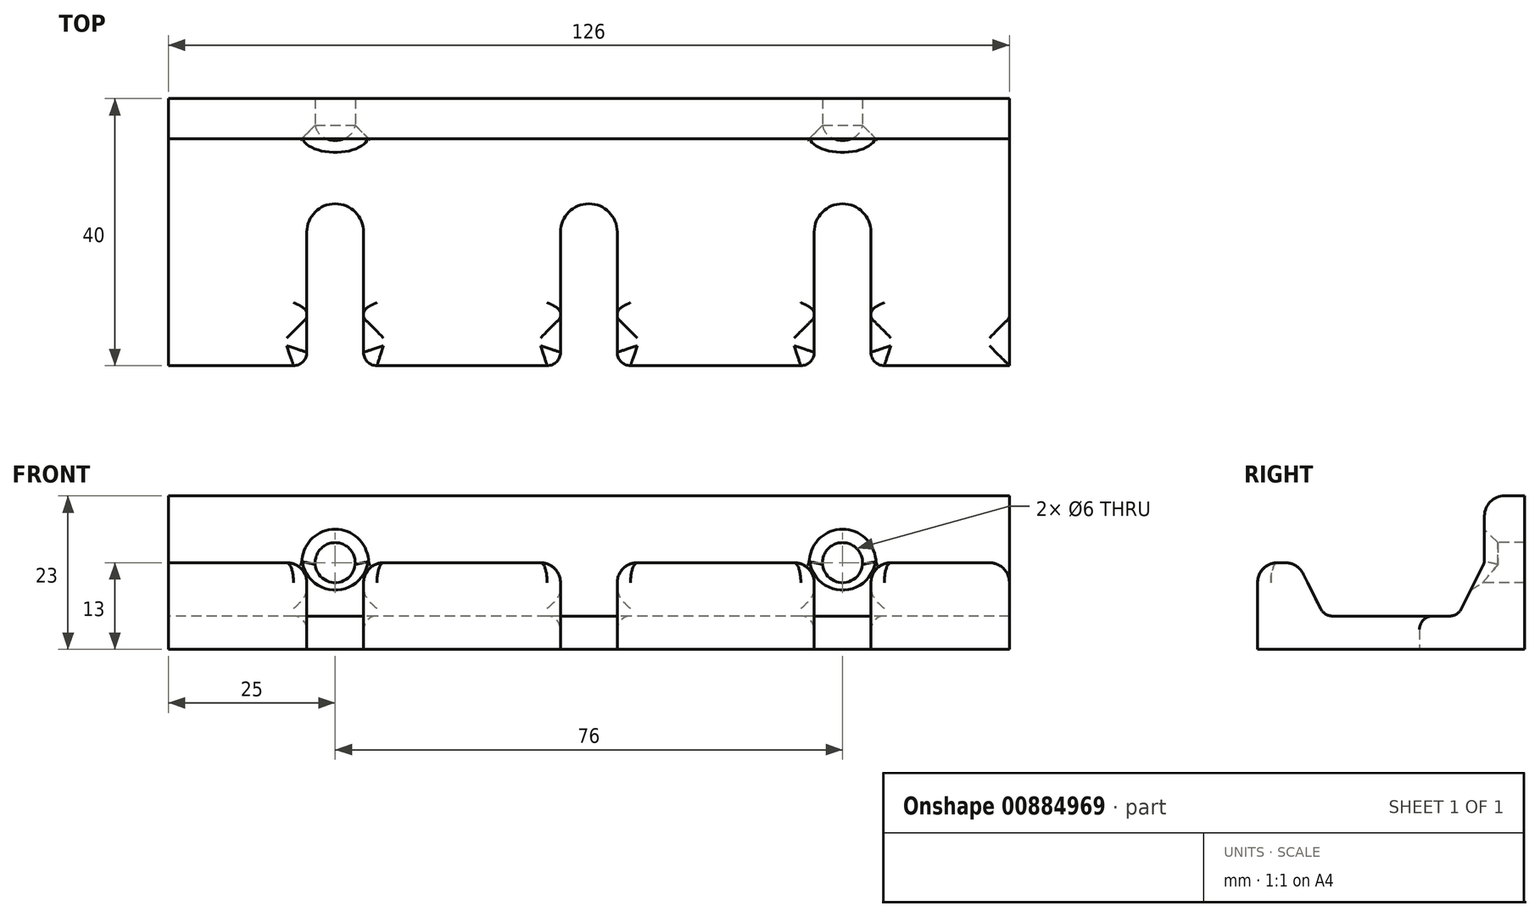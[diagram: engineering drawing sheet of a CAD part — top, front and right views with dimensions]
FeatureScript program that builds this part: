
annotation { "Feature Type Name" : "Feature", "Feature Type Description" : "" }
export const myFeature = defineFeature(function(context is Context, id is Id, definition is map)
    precondition{}
    {
        {
            var Q0;
            Q0=qCreatedBy(makeId("Top.planeOp"),FACE);
            var sketch = newSketch(context, id + "F0", { "sketchPlane" : qUnion([Q0])});
            skLineSegment(sketch, "E0.bottom", {"start": v(-63, 20) * mm, "end": v(63, 20) * mm});
            skLineSegment(sketch, "E0.top", {"start": v(-63, -20) * mm, "end": v(63, -20) * mm});
            skLineSegment(sketch, "E0.left", {"start": v(-63, 20) * mm, "end": v(-63, -20) * mm});
            skLineSegment(sketch, "E0.right", {"start": v(63, 20) * mm, "end": v(63, -20) * mm});
            skPoint(sketch, "E0.middle", {"position": v(0, 0) * mm});
            skSolve(sketch);
        }
        {
            var Q0;
            Q0=makeQuery(id+"F0.imprint","IMPRINT",FACE,{"disambiguationData":[TD([[makeQuery(id+"F0.imprint","IMPRINT",EDGE,{"derivedFrom":sQuery(id+"F0.wireOp",EDGE,"E0.bottom")}),-1.0]])]});
            extrude(context, id + "F1", {"entities" : qUnion([Q0]), "depth" : 5 * mm, "offsetDistance" : 25 * mm});
        }
        {
            var Q0;
            Q0=makeQuery(id+"F1.opExtrude","CAP_FACE",FACE,{"disambiguationData":[OSD([sQuery(id+"F0.wireOp",EDGE,"E0.bottom"),sQuery(id+"F0.wireOp",EDGE,"E0.top"),sQuery(id+"F0.wireOp",EDGE,"E0.left"),sQuery(id+"F0.wireOp",EDGE,"E0.right")])],"isStart":false});
            var sketch = newSketch(context, id + "F2", { "sketchPlane" : qUnion([Q0])});
            skLineSegment(sketch, "E1.bottom", {"start": v(-63, 10) * mm, "end": v(63, 10) * mm});
            skLineSegment(sketch, "E1.top", {"start": v(-63, -10) * mm, "end": v(63, -10) * mm});
            skLineSegment(sketch, "E1.left", {"start": v(-63, 10) * mm, "end": v(-63, -10) * mm});
            skLineSegment(sketch, "E1.right", {"start": v(63, 10) * mm, "end": v(63, -10) * mm});
            skPoint(sketch, "E1.middle", {"position": v(0, 0) * mm});
            skLineSegment(sketch, "E2.bottom", {"start": v(-63, 20) * mm, "end": v(63, 20) * mm});
            skLineSegment(sketch, "E2.top", {"start": v(-63, -20) * mm, "end": v(63, -20) * mm});
            skLineSegment(sketch, "E2.left", {"start": v(-63, 20) * mm, "end": v(-63, -20) * mm});
            skLineSegment(sketch, "E2.right", {"start": v(63, 20) * mm, "end": v(63, -20) * mm});
            skSolve(sketch);
        }
        {
            var Q0;
            {var subQ0=sQuery(id+"F2.wireOp",EDGE,"E1.bottom");Q0=makeQuery(id+"F2.imprint","IMPRINT",FACE,{"disambiguationData":[TD([[makeQuery(id+"F2.imprint","IMPRINT",EDGE,{"derivedFrom":subQ0}),1.0]])]});}
            var Q1;
            {var subQ0=sQuery(id+"F2.wireOp",EDGE,"E1.top");Q1=makeQuery(id+"F2.imprint","IMPRINT",FACE,{"disambiguationData":[TD([[makeQuery(id+"F2.imprint","IMPRINT",EDGE,{"derivedFrom":subQ0}),-1.0]])]});}
            extrude(context, id + "F3", {"entities" : qUnion([Q0, Q1]), "operationType" : NewBodyOperationType.ADD, "depth" : 8 * mm, "offsetDistance" : 25 * mm});
        }
        {
            var Q0;
            Q0=makeQuery(id+"F3.opExtrude","CAP_EDGE",EDGE,{"disambiguationData":[OSD([sQuery(id+"F2.wireOp",EDGE,"E1.bottom")])],"isStart":false});
            chamfer(context, id + "F4", {"entities" : qUnion([Q0]), "chamferType" : ChamferType.TWO_OFFSETS, "width1" : 8 * mm, "oppositeDirection" : true, "width2" : 4 * mm});
        }
        {
            var Q0;
            Q0=makeQuery(id+"F3.opExtrude","CAP_EDGE",EDGE,{"disambiguationData":[OSD([sQuery(id+"F2.wireOp",EDGE,"E1.top")])],"isStart":false});
            chamfer(context, id + "F5", {"entities" : qUnion([Q0]), "chamferType" : ChamferType.TWO_OFFSETS, "width1" : 8 * mm, "oppositeDirection" : false, "width2" : 4 * mm, "tangentPropagation" : true});
        }
        {
            var Q0;
            Q0=makeQuery(id+"F0.imprint","IMPRINT",FACE,{"disambiguationData":[TD([[makeQuery(id+"F0.imprint","IMPRINT",EDGE,{"derivedFrom":sQuery(id+"F0.wireOp",EDGE,"E0.bottom")}),-1.0]])]});
            var sketch = newSketch(context, id + "F6", { "sketchPlane" : qUnion([Q0])});
            skCircle(sketch, "E3", {"center": v(-38, 0) * mm, "radius": 4.25 * mm});
            skCircle(sketch, "E4.1.0.0", {"center": v(0, 0) * mm, "radius": 4.25 * mm});
            skCircle(sketch, "E4.2.0.0", {"center": v(38, 0) * mm, "radius": 4.25 * mm});
            skLineSegment(sketch, "E4.direction1", {"start": v(-38, 0) * mm, "end": v(0, 0) * mm, "construction": true});
            skLineSegment(sketch, "E5", {"start": v(-33.75, 0) * mm, "end": v(-33.75, -25) * mm});
            skLineSegment(sketch, "E6", {"start": v(-42.25, 0) * mm, "end": v(-42.25, -25) * mm});
            skLineSegment(sketch, "E7", {"start": v(-4.25, 0) * mm, "end": v(-4.25, -25) * mm});
            skLineSegment(sketch, "E8", {"start": v(-80.14, 0) * mm, "end": v(82.26, 0) * mm, "construction": true});
            skLineSegment(sketch, "E9", {"start": v(4.25, 0) * mm, "end": v(4.25, -25) * mm});
            skLineSegment(sketch, "E10", {"start": v(33.75, 0) * mm, "end": v(33.75, -25) * mm});
            skLineSegment(sketch, "E11", {"start": v(42.25, 0) * mm, "end": v(42.25, -25) * mm});
            skLineSegment(sketch, "E12", {"start": v(-33.75, -25) * mm, "end": v(-42.25, -25) * mm});
            skLineSegment(sketch, "E13", {"start": v(-4.25, -25) * mm, "end": v(4.25, -25) * mm});
            skLineSegment(sketch, "E14", {"start": v(33.75, -25) * mm, "end": v(42.25, -25) * mm});
            skSolve(sketch);
        }
        {
            var Q0;
            Q0=qSketchRegion(id+"F6",true);
            extrude(context, id + "F7", {"entities" : qUnion([Q0]), "operationType" : NewBodyOperationType.REMOVE, "depth" : 25 * mm, "offsetDistance" : 25 * mm});
        }
        {
            var Q0;
            Q0=makeQuery(id+"F3.opExtrude","CAP_FACE",FACE,{"disambiguationData":[OSD([sQuery(id+"F2.wireOp",EDGE,"E1.bottom"),sQuery(id+"F2.wireOp",EDGE,"E2.bottom"),sQuery(id+"F2.wireOp",EDGE,"E2.left"),sQuery(id+"F2.wireOp",EDGE,"E2.right")])],"isStart":false});
            extrude(context, id + "F8", {"entities" : qUnion([Q0]), "operationType" : NewBodyOperationType.ADD, "depth" : 10 * mm, "offsetDistance" : 25 * mm});
        }
        {
            var Q0;
            Q0=makeQuery(id+"F8.opExtrude","SWEPT_FACE",FACE,{"disambiguationData":[OSD([sQuery(id+"F2.wireOp",EDGE,"E1.bottom"),sQuery(id+"F2.wireOp",EDGE,"E2.bottom"),sQuery(id+"F2.wireOp",EDGE,"E2.left"),sQuery(id+"F2.wireOp",EDGE,"E2.right")])]});
            var sketch = newSketch(context, id + "F9", { "sketchPlane" : qUnion([Q0])});
            skCircle(sketch, "E15", {"center": v(-38, 13) * mm, "radius": 3 * mm});
            skCircle(sketch, "E16", {"center": v(38, 13) * mm, "radius": 3 * mm});
            skSolve(sketch);
        }
        {
            var Q0;
            Q0=qSketchRegion(id+"F9",true);
            extrude(context, id + "F10", {"entities" : qUnion([Q0]), "operationType" : NewBodyOperationType.REMOVE, "oppositeDirection" : true, "depth" : 15 * mm, "offsetDistance" : 25 * mm, "hasSecondDirection" : true, "secondDirectionOppositeDirection" : false, "secondDirectionDepth" : 15 * mm});
        }
        {
            var Q0;
            Q0=makeQuery(id+"F10.boolean.opBoolean","INTERSECT",EDGE,{"derivedFrom":[makeQuery(id+"F4.opChamfer","BLEND_FACE",FACE,{"disambiguationData":[OSD([sQuery(id+"F2.wireOp",EDGE,"E1.bottom")])]}),makeQuery(id+"F10.opExtrude","SWEPT_FACE",FACE,{"disambiguationData":[OSD([sQuery(id+"F9.wireOp",EDGE,"E15")])]})]});
            var Q1;
            Q1=makeQuery(id+"F10.boolean.opBoolean","INTERSECT",EDGE,{"derivedFrom":[makeQuery(id+"F8.opExtrude","SWEPT_FACE",FACE,{"disambiguationData":[OSD([sQuery(id+"F2.wireOp",EDGE,"E1.bottom"),sQuery(id+"F2.wireOp",EDGE,"E2.bottom"),sQuery(id+"F2.wireOp",EDGE,"E2.left"),sQuery(id+"F2.wireOp",EDGE,"E2.right")])]}),makeQuery(id+"F10.opExtrude","SWEPT_FACE",FACE,{"disambiguationData":[OSD([sQuery(id+"F9.wireOp",EDGE,"E15")])]})]});
            var Q2;
            Q2=makeQuery(id+"F10.boolean.opBoolean","INTERSECT",EDGE,{"derivedFrom":[makeQuery(id+"F4.opChamfer","BLEND_FACE",FACE,{"disambiguationData":[OSD([sQuery(id+"F2.wireOp",EDGE,"E1.bottom")])]}),makeQuery(id+"F10.opExtrude","SWEPT_FACE",FACE,{"disambiguationData":[OSD([sQuery(id+"F9.wireOp",EDGE,"E16")])]})]});
            var Q3;
            Q3=makeQuery(id+"F10.boolean.opBoolean","INTERSECT",EDGE,{"derivedFrom":[makeQuery(id+"F8.opExtrude","SWEPT_FACE",FACE,{"disambiguationData":[OSD([sQuery(id+"F2.wireOp",EDGE,"E1.bottom"),sQuery(id+"F2.wireOp",EDGE,"E2.bottom"),sQuery(id+"F2.wireOp",EDGE,"E2.left"),sQuery(id+"F2.wireOp",EDGE,"E2.right")])]}),makeQuery(id+"F10.opExtrude","SWEPT_FACE",FACE,{"disambiguationData":[OSD([sQuery(id+"F9.wireOp",EDGE,"E16")])]})]});
            chamfer(context, id + "F11", {"entities" : qUnion([Q0, Q1, Q2, Q3]), "width" : 2 * mm, "tangentPropagation" : true});
        }
        {
            var Q0;
            Q0=makeQuery(id+"F7.boolean.opBoolean","INTERSECT",EDGE,{"derivedFrom":[makeQuery(id+"F1.opExtrude","CAP_FACE",FACE,{"disambiguationData":[OSD([sQuery(id+"F0.wireOp",EDGE,"E0.bottom"),sQuery(id+"F0.wireOp",EDGE,"E0.top"),sQuery(id+"F0.wireOp",EDGE,"E0.left"),sQuery(id+"F0.wireOp",EDGE,"E0.right")])],"isStart":false}),makeQuery(id+"F7.opExtrude","SWEPT_FACE",FACE,{"disambiguationData":[OSD([sQuery(id+"F6.wireOp",EDGE,"E6")])]})]});
            var Q1;
            Q1=makeQuery(id+"F7.boolean.opBoolean","INTERSECT",EDGE,{"derivedFrom":[makeQuery(id+"F1.opExtrude","CAP_FACE",FACE,{"disambiguationData":[OSD([sQuery(id+"F0.wireOp",EDGE,"E0.bottom"),sQuery(id+"F0.wireOp",EDGE,"E0.top"),sQuery(id+"F0.wireOp",EDGE,"E0.left"),sQuery(id+"F0.wireOp",EDGE,"E0.right")])],"isStart":false}),makeQuery(id+"F7.opExtrude","SWEPT_FACE",FACE,{"disambiguationData":[OSD([sQuery(id+"F6.wireOp",EDGE,"E3")])]})]});
            var Q2;
            Q2=makeQuery(id+"F7.boolean.opBoolean","INTERSECT",EDGE,{"derivedFrom":[makeQuery(id+"F1.opExtrude","CAP_FACE",FACE,{"disambiguationData":[OSD([sQuery(id+"F0.wireOp",EDGE,"E0.bottom"),sQuery(id+"F0.wireOp",EDGE,"E0.top"),sQuery(id+"F0.wireOp",EDGE,"E0.left"),sQuery(id+"F0.wireOp",EDGE,"E0.right")])],"isStart":false}),makeQuery(id+"F7.opExtrude","SWEPT_FACE",FACE,{"disambiguationData":[OSD([sQuery(id+"F6.wireOp",EDGE,"E5")])]})]});
            var Q3;
            Q3=makeQuery(id+"F7.boolean.opBoolean","INTERSECT",EDGE,{"derivedFrom":[makeQuery(id+"F1.opExtrude","CAP_FACE",FACE,{"disambiguationData":[OSD([sQuery(id+"F0.wireOp",EDGE,"E0.bottom"),sQuery(id+"F0.wireOp",EDGE,"E0.top"),sQuery(id+"F0.wireOp",EDGE,"E0.left"),sQuery(id+"F0.wireOp",EDGE,"E0.right")])],"isStart":false}),makeQuery(id+"F7.opExtrude","SWEPT_FACE",FACE,{"disambiguationData":[OSD([sQuery(id+"F6.wireOp",EDGE,"E7")])]})]});
            var Q4;
            Q4=makeQuery(id+"F7.boolean.opBoolean","INTERSECT",EDGE,{"derivedFrom":[makeQuery(id+"F1.opExtrude","CAP_FACE",FACE,{"disambiguationData":[OSD([sQuery(id+"F0.wireOp",EDGE,"E0.bottom"),sQuery(id+"F0.wireOp",EDGE,"E0.top"),sQuery(id+"F0.wireOp",EDGE,"E0.left"),sQuery(id+"F0.wireOp",EDGE,"E0.right")])],"isStart":false}),makeQuery(id+"F7.opExtrude","SWEPT_FACE",FACE,{"disambiguationData":[OSD([sQuery(id+"F6.wireOp",EDGE,"E4.1.0.0")])]})]});
            var Q5;
            Q5=makeQuery(id+"F7.boolean.opBoolean","INTERSECT",EDGE,{"derivedFrom":[makeQuery(id+"F1.opExtrude","CAP_FACE",FACE,{"disambiguationData":[OSD([sQuery(id+"F0.wireOp",EDGE,"E0.bottom"),sQuery(id+"F0.wireOp",EDGE,"E0.top"),sQuery(id+"F0.wireOp",EDGE,"E0.left"),sQuery(id+"F0.wireOp",EDGE,"E0.right")])],"isStart":false}),makeQuery(id+"F7.opExtrude","SWEPT_FACE",FACE,{"disambiguationData":[OSD([sQuery(id+"F6.wireOp",EDGE,"E9")])]})]});
            var Q6;
            Q6=makeQuery(id+"F7.boolean.opBoolean","INTERSECT",EDGE,{"derivedFrom":[makeQuery(id+"F1.opExtrude","CAP_FACE",FACE,{"disambiguationData":[OSD([sQuery(id+"F0.wireOp",EDGE,"E0.bottom"),sQuery(id+"F0.wireOp",EDGE,"E0.top"),sQuery(id+"F0.wireOp",EDGE,"E0.left"),sQuery(id+"F0.wireOp",EDGE,"E0.right")])],"isStart":false}),makeQuery(id+"F7.opExtrude","SWEPT_FACE",FACE,{"disambiguationData":[OSD([sQuery(id+"F6.wireOp",EDGE,"E10")])]})]});
            var Q7;
            Q7=makeQuery(id+"F7.boolean.opBoolean","INTERSECT",EDGE,{"derivedFrom":[makeQuery(id+"F1.opExtrude","CAP_FACE",FACE,{"disambiguationData":[OSD([sQuery(id+"F0.wireOp",EDGE,"E0.bottom"),sQuery(id+"F0.wireOp",EDGE,"E0.top"),sQuery(id+"F0.wireOp",EDGE,"E0.left"),sQuery(id+"F0.wireOp",EDGE,"E0.right")])],"isStart":false}),makeQuery(id+"F7.opExtrude","SWEPT_FACE",FACE,{"disambiguationData":[OSD([sQuery(id+"F6.wireOp",EDGE,"G8VrYlGx-egmG-YajN-Oarc-HGY43DwGvVPw")])]})]});
            var Q8;
            Q8=makeQuery(id+"F7.boolean.opBoolean","COPY",EDGE,{"derivedFrom":makeQuery(id+"F7.opExtrude","CAP_EDGE",EDGE,{"disambiguationData":[OSD([sQuery(id+"F6.wireOp",EDGE,"E5")])],"isStart":true})});
            var Q9;
            Q9=makeQuery(id+"F7.boolean.opBoolean","COPY",EDGE,{"derivedFrom":makeQuery(id+"F7.opExtrude","CAP_EDGE",EDGE,{"disambiguationData":[OSD([sQuery(id+"F6.wireOp",EDGE,"E9")])],"isStart":true})});
            var Q10;
            Q10=makeQuery(id+"F7.boolean.opBoolean","COPY",EDGE,{"derivedFrom":makeQuery(id+"F7.opExtrude","CAP_EDGE",EDGE,{"disambiguationData":[OSD([sQuery(id+"F6.wireOp",EDGE,"E11")])],"isStart":true})});
            var Q11;
            Q11=makeQuery(id+"F7.boolean.opBoolean","COPY",EDGE,{"derivedFrom":makeQuery(id+"F7.opExtrude","CAP_EDGE",EDGE,{"disambiguationData":[OSD([sQuery(id+"F6.wireOp",EDGE,"c489k1hw-giI0-qjXx-Yk1g-4kGI9rd1hbMV")])],"isStart":true})});
            var Q12;
            Q12=makeQuery(id+"F7.boolean.opBoolean","INTERSECT",EDGE,{"derivedFrom":[makeQuery(id+"F3.boolean.opBoolean","MERGE",FACE,{"derivedFrom":[makeQuery(id+"F1.opExtrude","SWEPT_FACE",FACE,{"disambiguationData":[OSD([sQuery(id+"F0.wireOp",EDGE,"E0.top")])]}),makeQuery(id+"F3.opExtrude","SWEPT_FACE",FACE,{"disambiguationData":[OSD([sQuery(id+"F2.wireOp",EDGE,"E2.top")])]})]}),makeQuery(id+"F7.opExtrude","SWEPT_FACE",FACE,{"disambiguationData":[OSD([sQuery(id+"F6.wireOp",EDGE,"E6")])]})]});
            var Q13;
            Q13=makeQuery(id+"F7.boolean.opBoolean","INTERSECT",EDGE,{"derivedFrom":[makeQuery(id+"F3.boolean.opBoolean","MERGE",FACE,{"derivedFrom":[makeQuery(id+"F1.opExtrude","SWEPT_FACE",FACE,{"disambiguationData":[OSD([sQuery(id+"F0.wireOp",EDGE,"E0.top")])]}),makeQuery(id+"F3.opExtrude","SWEPT_FACE",FACE,{"disambiguationData":[OSD([sQuery(id+"F2.wireOp",EDGE,"E2.top")])]})]}),makeQuery(id+"F7.opExtrude","SWEPT_FACE",FACE,{"disambiguationData":[OSD([sQuery(id+"F6.wireOp",EDGE,"E5")])]})]});
            var Q14;
            Q14=makeQuery(id+"F7.boolean.opBoolean","INTERSECT",EDGE,{"derivedFrom":[makeQuery(id+"F3.boolean.opBoolean","MERGE",FACE,{"derivedFrom":[makeQuery(id+"F1.opExtrude","SWEPT_FACE",FACE,{"disambiguationData":[OSD([sQuery(id+"F0.wireOp",EDGE,"E0.top")])]}),makeQuery(id+"F3.opExtrude","SWEPT_FACE",FACE,{"disambiguationData":[OSD([sQuery(id+"F2.wireOp",EDGE,"E2.top")])]})]}),makeQuery(id+"F7.opExtrude","SWEPT_FACE",FACE,{"disambiguationData":[OSD([sQuery(id+"F6.wireOp",EDGE,"E7")])]})]});
            var Q15;
            Q15=makeQuery(id+"F7.boolean.opBoolean","INTERSECT",EDGE,{"derivedFrom":[makeQuery(id+"F3.boolean.opBoolean","MERGE",FACE,{"derivedFrom":[makeQuery(id+"F1.opExtrude","SWEPT_FACE",FACE,{"disambiguationData":[OSD([sQuery(id+"F0.wireOp",EDGE,"E0.top")])]}),makeQuery(id+"F3.opExtrude","SWEPT_FACE",FACE,{"disambiguationData":[OSD([sQuery(id+"F2.wireOp",EDGE,"E2.top")])]})]}),makeQuery(id+"F7.opExtrude","SWEPT_FACE",FACE,{"disambiguationData":[OSD([sQuery(id+"F6.wireOp",EDGE,"E9")])]})]});
            var Q16;
            Q16=makeQuery(id+"F7.boolean.opBoolean","INTERSECT",EDGE,{"derivedFrom":[makeQuery(id+"F3.boolean.opBoolean","MERGE",FACE,{"derivedFrom":[makeQuery(id+"F1.opExtrude","SWEPT_FACE",FACE,{"disambiguationData":[OSD([sQuery(id+"F0.wireOp",EDGE,"E0.top")])]}),makeQuery(id+"F3.opExtrude","SWEPT_FACE",FACE,{"disambiguationData":[OSD([sQuery(id+"F2.wireOp",EDGE,"E2.top")])]})]}),makeQuery(id+"F7.opExtrude","SWEPT_FACE",FACE,{"disambiguationData":[OSD([sQuery(id+"F6.wireOp",EDGE,"E10")])]})]});
            var Q17;
            Q17=makeQuery(id+"F7.boolean.opBoolean","INTERSECT",EDGE,{"derivedFrom":[makeQuery(id+"F3.boolean.opBoolean","MERGE",FACE,{"derivedFrom":[makeQuery(id+"F1.opExtrude","SWEPT_FACE",FACE,{"disambiguationData":[OSD([sQuery(id+"F0.wireOp",EDGE,"E0.top")])]}),makeQuery(id+"F3.opExtrude","SWEPT_FACE",FACE,{"disambiguationData":[OSD([sQuery(id+"F2.wireOp",EDGE,"E2.top")])]})]}),makeQuery(id+"F7.opExtrude","SWEPT_FACE",FACE,{"disambiguationData":[OSD([sQuery(id+"F6.wireOp",EDGE,"E11")])]})]});
            var Q18;
            Q18=makeQuery(id+"F7.boolean.opBoolean","INTERSECT",EDGE,{"derivedFrom":[makeQuery(id+"F3.boolean.opBoolean","MERGE",FACE,{"derivedFrom":[makeQuery(id+"F1.opExtrude","SWEPT_FACE",FACE,{"disambiguationData":[OSD([sQuery(id+"F0.wireOp",EDGE,"E0.top")])]}),makeQuery(id+"F3.opExtrude","SWEPT_FACE",FACE,{"disambiguationData":[OSD([sQuery(id+"F2.wireOp",EDGE,"E2.top")])]})]}),makeQuery(id+"F7.opExtrude","SWEPT_FACE",FACE,{"disambiguationData":[OSD([sQuery(id+"F6.wireOp",EDGE,"G8VrYlGx-egmG-YajN-Oarc-HGY43DwGvVPw")])]})]});
            var Q19;
            Q19=makeQuery(id+"F7.boolean.opBoolean","INTERSECT",EDGE,{"derivedFrom":[makeQuery(id+"F3.boolean.opBoolean","MERGE",FACE,{"derivedFrom":[makeQuery(id+"F1.opExtrude","SWEPT_FACE",FACE,{"disambiguationData":[OSD([sQuery(id+"F0.wireOp",EDGE,"E0.top")])]}),makeQuery(id+"F3.opExtrude","SWEPT_FACE",FACE,{"disambiguationData":[OSD([sQuery(id+"F2.wireOp",EDGE,"E2.top")])]})]}),makeQuery(id+"F7.opExtrude","SWEPT_FACE",FACE,{"disambiguationData":[OSD([sQuery(id+"F6.wireOp",EDGE,"c489k1hw-giI0-qjXx-Yk1g-4kGI9rd1hbMV")])]})]});
            var Q20;
            {var subQ0=makeQuery(id+"F1.opExtrude","CAP_FACE",FACE,{"disambiguationData":[OSD([sQuery(id+"F0.wireOp",EDGE,"E0.bottom"),sQuery(id+"F0.wireOp",EDGE,"E0.top"),sQuery(id+"F0.wireOp",EDGE,"E0.left"),sQuery(id+"F0.wireOp",EDGE,"E0.right")])],"isStart":false});var subQ1=sQuery(id+"F2.wireOp",EDGE,"E1.top");Q20=makeQuery(id+"F7.boolean.opBoolean","SPLIT",EDGE,{"disambiguationData":[TD([makeQuery(id+"F7.opExtrude","SWEPT_FACE",FACE,{"disambiguationData":[OSD([sQuery(id+"F6.wireOp",EDGE,"E9")])]})])],"derivedFrom":makeQuery(id+"F5.opChamfer","BLEND_EDGE",EDGE,{"blendedFrom":[makeQuery(id+"F3.opExtrude","CAP_EDGE",EDGE,{"disambiguationData":[OSD([subQ1])],"isStart":false}),subQ0],"blendedInto":[subQ0]})});}
            var Q21;
            {var subQ0=makeQuery(id+"F1.opExtrude","CAP_FACE",FACE,{"disambiguationData":[OSD([sQuery(id+"F0.wireOp",EDGE,"E0.bottom"),sQuery(id+"F0.wireOp",EDGE,"E0.top"),sQuery(id+"F0.wireOp",EDGE,"E0.left"),sQuery(id+"F0.wireOp",EDGE,"E0.right")])],"isStart":false});var subQ1=sQuery(id+"F2.wireOp",EDGE,"E1.top");Q21=makeQuery(id+"F7.boolean.opBoolean","SPLIT",EDGE,{"disambiguationData":[TD([makeQuery(id+"F7.opExtrude","SWEPT_FACE",FACE,{"disambiguationData":[OSD([sQuery(id+"F6.wireOp",EDGE,"E5")])]})])],"derivedFrom":makeQuery(id+"F5.opChamfer","BLEND_EDGE",EDGE,{"blendedFrom":[makeQuery(id+"F3.opExtrude","CAP_EDGE",EDGE,{"disambiguationData":[OSD([subQ1])],"isStart":false}),subQ0],"blendedInto":[subQ0]})});}
            var Q22;
            {var subQ1=sQuery(id+"F0.wireOp",EDGE,"E0.left");var subQ2=sQuery(id+"F2.wireOp",EDGE,"E1.top");var subQ3=makeQuery(id+"F1.opExtrude","CAP_FACE",FACE,{"disambiguationData":[OSD([sQuery(id+"F0.wireOp",EDGE,"E0.bottom"),sQuery(id+"F0.wireOp",EDGE,"E0.top"),subQ1,sQuery(id+"F0.wireOp",EDGE,"E0.right")])],"isStart":false});Q22=makeQuery(id+"F7.boolean.opBoolean","SPLIT",EDGE,{"disambiguationData":[TD([makeQuery(id+"F1.opExtrude","SWEPT_FACE",FACE,{"disambiguationData":[OSD([subQ1])]})])],"derivedFrom":makeQuery(id+"F5.opChamfer","BLEND_EDGE",EDGE,{"blendedFrom":[makeQuery(id+"F3.opExtrude","CAP_EDGE",EDGE,{"disambiguationData":[OSD([subQ2])],"isStart":false}),subQ3],"blendedInto":[subQ3]})});}
            var Q23;
            {var subQ0=makeQuery(id+"F1.opExtrude","CAP_FACE",FACE,{"disambiguationData":[OSD([sQuery(id+"F0.wireOp",EDGE,"E0.bottom"),sQuery(id+"F0.wireOp",EDGE,"E0.top"),sQuery(id+"F0.wireOp",EDGE,"E0.left"),sQuery(id+"F0.wireOp",EDGE,"E0.right")])],"isStart":false});var subQ1=sQuery(id+"F2.wireOp",EDGE,"E1.top");Q23=makeQuery(id+"F7.boolean.opBoolean","SPLIT",EDGE,{"disambiguationData":[TD([makeQuery(id+"F7.opExtrude","SWEPT_FACE",FACE,{"disambiguationData":[OSD([sQuery(id+"F6.wireOp",EDGE,"E11")])]})])],"derivedFrom":makeQuery(id+"F5.opChamfer","BLEND_EDGE",EDGE,{"blendedFrom":[makeQuery(id+"F3.opExtrude","CAP_EDGE",EDGE,{"disambiguationData":[OSD([subQ1])],"isStart":false}),subQ0],"blendedInto":[subQ0]})});}
            var Q24;
            {var subQ1=sQuery(id+"F2.wireOp",EDGE,"E1.top");var subQ2=sQuery(id+"F0.wireOp",EDGE,"E0.right");var subQ3=makeQuery(id+"F1.opExtrude","CAP_FACE",FACE,{"disambiguationData":[OSD([sQuery(id+"F0.wireOp",EDGE,"E0.bottom"),sQuery(id+"F0.wireOp",EDGE,"E0.top"),sQuery(id+"F0.wireOp",EDGE,"E0.left"),subQ2])],"isStart":false});Q24=makeQuery(id+"F7.boolean.opBoolean","SPLIT",EDGE,{"disambiguationData":[TD([makeQuery(id+"F1.opExtrude","SWEPT_FACE",FACE,{"disambiguationData":[OSD([subQ2])]})])],"derivedFrom":makeQuery(id+"F5.opChamfer","BLEND_EDGE",EDGE,{"blendedFrom":[makeQuery(id+"F3.opExtrude","CAP_EDGE",EDGE,{"disambiguationData":[OSD([subQ1])],"isStart":false}),subQ3],"blendedInto":[subQ3]})});}
            var Q25;
            Q25=makeQuery(id+"F4.opChamfer","BLEND_EDGE",EDGE,{"blendedFrom":[makeQuery(id+"F3.opExtrude","CAP_EDGE",EDGE,{"disambiguationData":[OSD([sQuery(id+"F2.wireOp",EDGE,"E1.bottom")])],"isStart":false}),makeQuery(id+"F1.opExtrude","CAP_FACE",FACE,{"disambiguationData":[OSD([sQuery(id+"F0.wireOp",EDGE,"E0.bottom"),sQuery(id+"F0.wireOp",EDGE,"E0.top"),sQuery(id+"F0.wireOp",EDGE,"E0.left"),sQuery(id+"F0.wireOp",EDGE,"E0.right")])],"isStart":false})],"blendedInto":[makeQuery(id+"F1.opExtrude","CAP_FACE",FACE,{"disambiguationData":[OSD([sQuery(id+"F0.wireOp",EDGE,"E0.bottom"),sQuery(id+"F0.wireOp",EDGE,"E0.top"),sQuery(id+"F0.wireOp",EDGE,"E0.left"),sQuery(id+"F0.wireOp",EDGE,"E0.right")])],"isStart":false})]});
            var Q26;
            {var subQ0=sQuery(id+"F2.wireOp",EDGE,"E1.bottom");var subQ1=sQuery(id+"F2.wireOp",EDGE,"E2.left");var subQ2=sQuery(id+"F2.wireOp",EDGE,"E2.bottom");var subQ3=sQuery(id+"F2.wireOp",EDGE,"E2.right");Q26=makeQuery(id+"F10.boolean.opBoolean","SPLIT",EDGE,{"disambiguationData":[TD([makeQuery(id+"F1.opExtrude","SWEPT_FACE",FACE,{"disambiguationData":[OSD([sQuery(id+"F0.wireOp",EDGE,"E0.left")])]}),makeQuery(id+"F3.opExtrude","SWEPT_FACE",FACE,{"disambiguationData":[OSD([subQ1]),TDD([makeQuery(id+"F2.imprint","IMPRINT",EDGE,{"disambiguationData":[TD([[makeQuery(id+"F2.imprint","INTERSECT",VERTEX,{"derivedFrom":[subQ2,subQ1]}),-1.0]])],"derivedFrom":subQ1})])]}),makeQuery(id+"F3.opExtrude","SWEPT_FACE",FACE,{"disambiguationData":[OSD([subQ1]),TDD([makeQuery(id+"F2.imprint","IMPRINT",EDGE,{"disambiguationData":[TD([[makeQuery(id+"F2.imprint","INTERSECT",VERTEX,{"derivedFrom":[sQuery(id+"F2.wireOp",EDGE,"E2.top"),subQ1]}),1.0]])],"derivedFrom":subQ1})])]}),makeQuery(id+"F4.opChamfer","BLEND_FACE",FACE,{"disambiguationData":[OSD([subQ0])]}),makeQuery(id+"F8.opExtrude","SWEPT_FACE",FACE,{"disambiguationData":[OSD([subQ0,subQ2,subQ1,subQ3])]}),makeQuery(id+"F8.opExtrude","SWEPT_FACE",FACE,{"disambiguationData":[OSD([subQ1])]}),makeQuery(id+"F10.opExtrude","SWEPT_FACE",FACE,{"disambiguationData":[OSD([sQuery(id+"F9.wireOp",EDGE,"E15")])]})])],"derivedFrom":makeQuery(id+"F8.boolean.opBoolean","MERGE",EDGE,{"derivedFrom":[makeQuery(id+"F4.opChamfer","BLEND_EDGE",EDGE,{"blendedFrom":[makeQuery(id+"F3.opExtrude","CAP_EDGE",EDGE,{"disambiguationData":[OSD([subQ0])],"isStart":false}),makeQuery(id+"F3.opExtrude","CAP_FACE",FACE,{"disambiguationData":[OSD([subQ0,subQ2,subQ1,subQ3])],"isStart":false})],"blendedInto":[makeQuery(id+"F3.opExtrude","CAP_FACE",FACE,{"disambiguationData":[OSD([subQ0,subQ2,subQ1,subQ3])],"isStart":false})]}),makeQuery(id+"F8.opExtrude","CAP_EDGE",EDGE,{"disambiguationData":[OSD([subQ0,subQ2,subQ1,subQ3])],"isStart":true})]})});}
            var Q27;
            {var subQ0=sQuery(id+"F2.wireOp",EDGE,"E1.bottom");var subQ1=sQuery(id+"F2.wireOp",EDGE,"E2.right");var subQ2=sQuery(id+"F2.wireOp",EDGE,"E2.left");var subQ3=sQuery(id+"F2.wireOp",EDGE,"E2.bottom");Q27=makeQuery(id+"F10.boolean.opBoolean","SPLIT",EDGE,{"disambiguationData":[TD([makeQuery(id+"F4.opChamfer","BLEND_FACE",FACE,{"disambiguationData":[OSD([subQ0])]}),makeQuery(id+"F8.opExtrude","SWEPT_FACE",FACE,{"disambiguationData":[OSD([subQ0,subQ3,subQ2,subQ1])]}),makeQuery(id+"F10.opExtrude","SWEPT_FACE",FACE,{"disambiguationData":[OSD([sQuery(id+"F9.wireOp",EDGE,"E15")])]}),makeQuery(id+"F10.opExtrude","SWEPT_FACE",FACE,{"disambiguationData":[OSD([sQuery(id+"F9.wireOp",EDGE,"E16")])]})])],"derivedFrom":makeQuery(id+"F8.boolean.opBoolean","MERGE",EDGE,{"derivedFrom":[makeQuery(id+"F4.opChamfer","BLEND_EDGE",EDGE,{"blendedFrom":[makeQuery(id+"F3.opExtrude","CAP_EDGE",EDGE,{"disambiguationData":[OSD([subQ0])],"isStart":false}),makeQuery(id+"F3.opExtrude","CAP_FACE",FACE,{"disambiguationData":[OSD([subQ0,subQ3,subQ2,subQ1])],"isStart":false})],"blendedInto":[makeQuery(id+"F3.opExtrude","CAP_FACE",FACE,{"disambiguationData":[OSD([subQ0,subQ3,subQ2,subQ1])],"isStart":false})]}),makeQuery(id+"F8.opExtrude","CAP_EDGE",EDGE,{"disambiguationData":[OSD([subQ0,subQ3,subQ2,subQ1])],"isStart":true})]})});}
            var Q28;
            {var subQ0=sQuery(id+"F2.wireOp",EDGE,"E2.right");var subQ1=sQuery(id+"F2.wireOp",EDGE,"E2.bottom");var subQ2=sQuery(id+"F2.wireOp",EDGE,"E1.bottom");var subQ3=sQuery(id+"F2.wireOp",EDGE,"E2.left");Q28=makeQuery(id+"F10.boolean.opBoolean","SPLIT",EDGE,{"disambiguationData":[TD([makeQuery(id+"F1.opExtrude","SWEPT_FACE",FACE,{"disambiguationData":[OSD([sQuery(id+"F0.wireOp",EDGE,"E0.right")])]}),makeQuery(id+"F3.opExtrude","SWEPT_FACE",FACE,{"disambiguationData":[OSD([subQ0]),TDD([makeQuery(id+"F2.imprint","IMPRINT",EDGE,{"disambiguationData":[TD([[makeQuery(id+"F2.imprint","INTERSECT",VERTEX,{"derivedFrom":[subQ1,subQ0]}),-1.0]])],"derivedFrom":subQ0})])]}),makeQuery(id+"F3.opExtrude","SWEPT_FACE",FACE,{"disambiguationData":[OSD([subQ0]),TDD([makeQuery(id+"F2.imprint","IMPRINT",EDGE,{"disambiguationData":[TD([[makeQuery(id+"F2.imprint","INTERSECT",VERTEX,{"derivedFrom":[sQuery(id+"F2.wireOp",EDGE,"E2.top"),subQ0]}),1.0]])],"derivedFrom":subQ0})])]}),makeQuery(id+"F4.opChamfer","BLEND_FACE",FACE,{"disambiguationData":[OSD([subQ2])]}),makeQuery(id+"F8.opExtrude","SWEPT_FACE",FACE,{"disambiguationData":[OSD([subQ2,subQ1,subQ3,subQ0])]}),makeQuery(id+"F8.opExtrude","SWEPT_FACE",FACE,{"disambiguationData":[OSD([subQ0])]}),makeQuery(id+"F10.opExtrude","SWEPT_FACE",FACE,{"disambiguationData":[OSD([sQuery(id+"F9.wireOp",EDGE,"E16")])]})])],"derivedFrom":makeQuery(id+"F8.boolean.opBoolean","MERGE",EDGE,{"derivedFrom":[makeQuery(id+"F4.opChamfer","BLEND_EDGE",EDGE,{"blendedFrom":[makeQuery(id+"F3.opExtrude","CAP_EDGE",EDGE,{"disambiguationData":[OSD([subQ2])],"isStart":false}),makeQuery(id+"F3.opExtrude","CAP_FACE",FACE,{"disambiguationData":[OSD([subQ2,subQ1,subQ3,subQ0])],"isStart":false})],"blendedInto":[makeQuery(id+"F3.opExtrude","CAP_FACE",FACE,{"disambiguationData":[OSD([subQ2,subQ1,subQ3,subQ0])],"isStart":false})]}),makeQuery(id+"F8.opExtrude","CAP_EDGE",EDGE,{"disambiguationData":[OSD([subQ2,subQ1,subQ3,subQ0])],"isStart":true})]})});}
            fillet(context, id + "F12", {"entities" : qUnion([Q0, Q1, Q2, Q3, Q4, Q5, Q6, Q7, Q8, Q9, Q10, Q11, Q12, Q13, Q14, Q15, Q16, Q17, Q18, Q19, Q20, Q21, Q22, Q23, Q24, Q25, Q26, Q27, Q28]), "radius" : 2 * mm, "tangentPropagation" : true, "allowEdgeOverflow" : false});
        }
        {
            var Q0;
            Q0=makeQuery(id+"F8.opExtrude","CAP_EDGE",EDGE,{"disambiguationData":[OSD([sQuery(id+"F2.wireOp",EDGE,"E1.bottom"),sQuery(id+"F2.wireOp",EDGE,"E2.bottom"),sQuery(id+"F2.wireOp",EDGE,"E2.left"),sQuery(id+"F2.wireOp",EDGE,"E2.right")])],"isStart":false});
            var Q1;
            {var subQ0=sQuery(id+"F2.wireOp",EDGE,"E2.left");var subQ1=sQuery(id+"F2.wireOp",EDGE,"E2.top");var subQ2=sQuery(id+"F2.wireOp",EDGE,"E1.top");var subQ3=makeQuery(id+"F3.opExtrude","CAP_FACE",FACE,{"disambiguationData":[OSD([subQ2,subQ1,subQ0,sQuery(id+"F2.wireOp",EDGE,"E2.right")])],"isStart":false});Q1=makeQuery(id+"F7.boolean.opBoolean","SPLIT",EDGE,{"disambiguationData":[TD([makeQuery(id+"F1.opExtrude","SWEPT_FACE",FACE,{"disambiguationData":[OSD([sQuery(id+"F0.wireOp",EDGE,"E0.left")])]})])],"derivedFrom":makeQuery(id+"F5.opChamfer","BLEND_EDGE",EDGE,{"blendedFrom":[makeQuery(id+"F3.opExtrude","CAP_EDGE",EDGE,{"disambiguationData":[OSD([subQ2])],"isStart":false}),subQ3],"blendedInto":[subQ3]})});}
            var Q2;
            {var subQ0=sQuery(id+"F2.wireOp",EDGE,"E2.top");Q2=makeQuery(id+"F7.boolean.opBoolean","SPLIT",EDGE,{"disambiguationData":[TD([makeQuery(id+"F1.opExtrude","SWEPT_FACE",FACE,{"disambiguationData":[OSD([sQuery(id+"F0.wireOp",EDGE,"E0.left")])]})])],"derivedFrom":makeQuery(id+"F3.opExtrude","CAP_EDGE",EDGE,{"disambiguationData":[OSD([subQ0])],"isStart":false})});}
            var Q3;
            {var subQ0=sQuery(id+"F2.wireOp",EDGE,"E2.top");var subQ1=sQuery(id+"F2.wireOp",EDGE,"E1.top");Q3=makeQuery(id+"F7.boolean.opBoolean","SPLIT",FACE,{"disambiguationData":[TD([makeQuery(id+"F7.opExtrude","SWEPT_FACE",FACE,{"disambiguationData":[OSD([sQuery(id+"F6.wireOp",EDGE,"E5")])]})])],"derivedFrom":makeQuery(id+"F3.opExtrude","CAP_FACE",FACE,{"disambiguationData":[OSD([subQ1,subQ0,sQuery(id+"F2.wireOp",EDGE,"E2.left"),sQuery(id+"F2.wireOp",EDGE,"E2.right")])],"isStart":false})});}
            var Q4;
            {var subQ0=sQuery(id+"F2.wireOp",EDGE,"E1.top");var subQ1=sQuery(id+"F2.wireOp",EDGE,"E2.top");Q4=makeQuery(id+"F7.boolean.opBoolean","SPLIT",FACE,{"disambiguationData":[TD([makeQuery(id+"F7.opExtrude","SWEPT_FACE",FACE,{"disambiguationData":[OSD([sQuery(id+"F6.wireOp",EDGE,"E9")])]})])],"derivedFrom":makeQuery(id+"F3.opExtrude","CAP_FACE",FACE,{"disambiguationData":[OSD([subQ0,subQ1,sQuery(id+"F2.wireOp",EDGE,"E2.left"),sQuery(id+"F2.wireOp",EDGE,"E2.right")])],"isStart":false})});}
            var Q5;
            {var subQ0=sQuery(id+"F2.wireOp",EDGE,"E1.top");var subQ1=sQuery(id+"F2.wireOp",EDGE,"E2.top");Q5=makeQuery(id+"F7.boolean.opBoolean","SPLIT",FACE,{"disambiguationData":[TD([makeQuery(id+"F7.opExtrude","SWEPT_FACE",FACE,{"disambiguationData":[OSD([sQuery(id+"F6.wireOp",EDGE,"E11")])]})])],"derivedFrom":makeQuery(id+"F3.opExtrude","CAP_FACE",FACE,{"disambiguationData":[OSD([subQ0,subQ1,sQuery(id+"F2.wireOp",EDGE,"E2.left"),sQuery(id+"F2.wireOp",EDGE,"E2.right")])],"isStart":false})});}
            var Q6;
            {var subQ0=sQuery(id+"F2.wireOp",EDGE,"E2.right");var subQ1=sQuery(id+"F2.wireOp",EDGE,"E2.top");var subQ2=sQuery(id+"F2.wireOp",EDGE,"E1.top");var subQ3=makeQuery(id+"F3.opExtrude","CAP_FACE",FACE,{"disambiguationData":[OSD([subQ2,subQ1,sQuery(id+"F2.wireOp",EDGE,"E2.left"),subQ0])],"isStart":false});Q6=makeQuery(id+"F7.boolean.opBoolean","SPLIT",EDGE,{"disambiguationData":[TD([makeQuery(id+"F1.opExtrude","SWEPT_FACE",FACE,{"disambiguationData":[OSD([sQuery(id+"F0.wireOp",EDGE,"E0.right")])]})])],"derivedFrom":makeQuery(id+"F5.opChamfer","BLEND_EDGE",EDGE,{"blendedFrom":[makeQuery(id+"F3.opExtrude","CAP_EDGE",EDGE,{"disambiguationData":[OSD([subQ2])],"isStart":false}),subQ3],"blendedInto":[subQ3]})});}
            var Q7;
            {var subQ0=sQuery(id+"F2.wireOp",EDGE,"E2.top");Q7=makeQuery(id+"F7.boolean.opBoolean","SPLIT",EDGE,{"disambiguationData":[TD([makeQuery(id+"F1.opExtrude","SWEPT_FACE",FACE,{"disambiguationData":[OSD([sQuery(id+"F0.wireOp",EDGE,"E0.right")])]})])],"derivedFrom":makeQuery(id+"F3.opExtrude","CAP_EDGE",EDGE,{"disambiguationData":[OSD([subQ0])],"isStart":false})});}
            fillet(context, id + "F13", {"entities" : qUnion([Q0, Q1, Q2, Q3, Q4, Q5, Q6, Q7]), "radius" : 3 * mm, "tangentPropagation" : true, "allowEdgeOverflow" : false});
        }
    });
